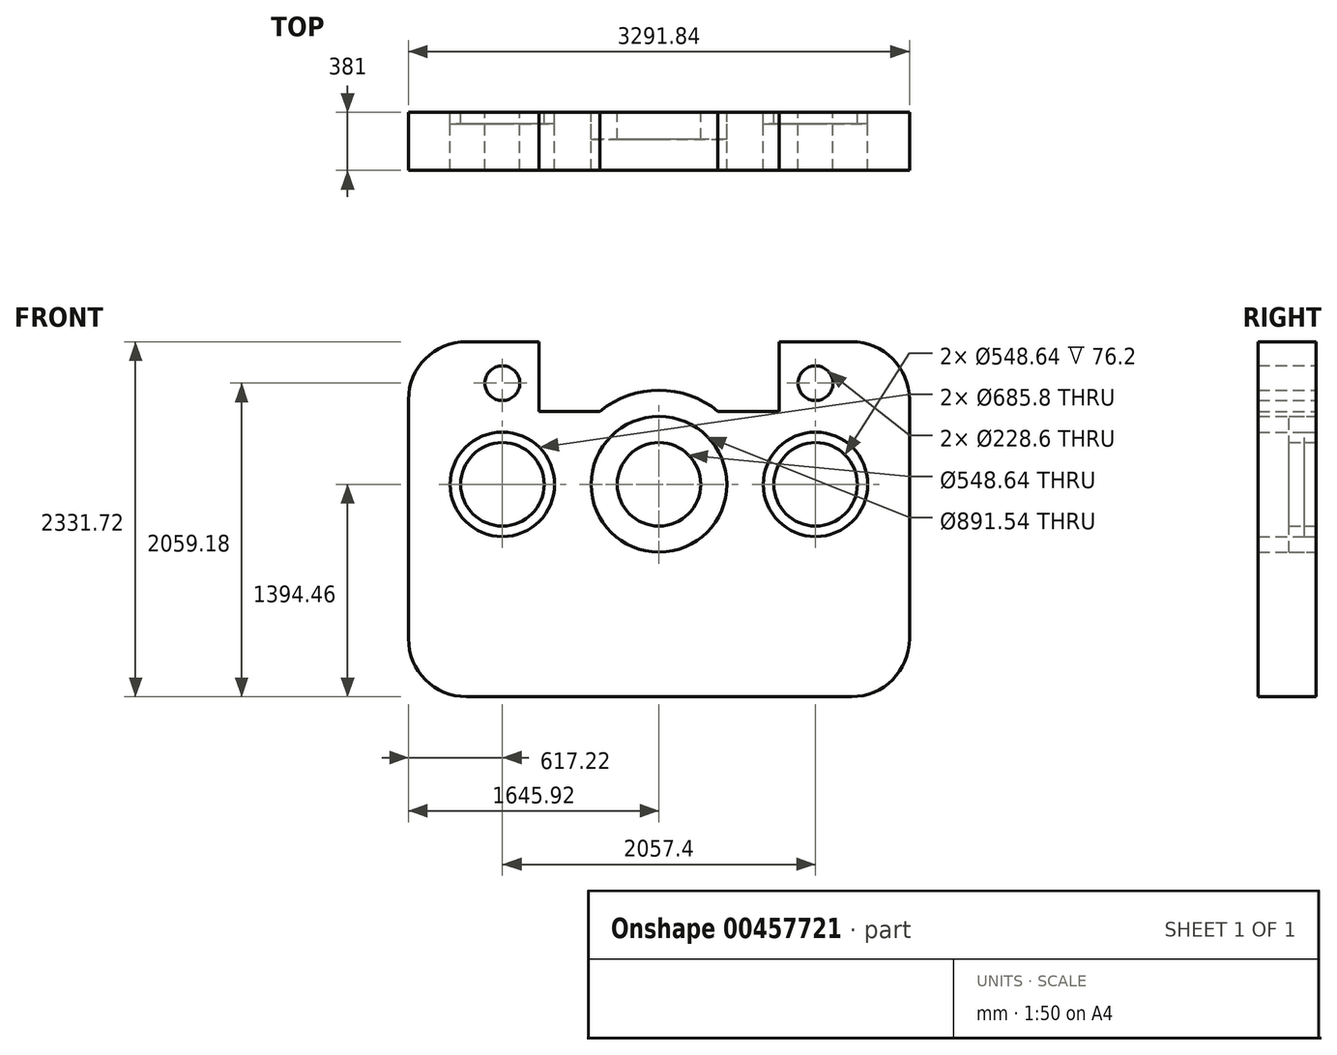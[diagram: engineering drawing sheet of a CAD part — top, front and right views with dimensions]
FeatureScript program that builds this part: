
annotation { "Feature Type Name" : "Feature", "Feature Type Description" : "" }
export const myFeature = defineFeature(function(context is Context, id is Id, definition is map)
    precondition{}
    {
        {
            var Q0;
            Q0=qCreatedBy(makeId("Front.planeOp"),FACE);
            var sketch = newSketch(context, id + "F0", { "sketchPlane" : qUnion([Q0])});
            skLineSegment(sketch, "E0", {"start": v(0, 381) * mm, "end": v(0, 1950.72) * mm});
            skLineSegment(sketch, "E1", {"start": v(381, 0) * mm, "end": v(2910.84, 0) * mm});
            skLineSegment(sketch, "E2", {"start": v(3291.84, 381) * mm, "end": v(3291.84, 1950.72) * mm});
            skArc(sketch, "E3", {"start": v(0, 381) * mm, "mid": v(111.6, 111.6) * mm, "end": v(381, 0) * mm});
            skArc(sketch, "E4", {"start": v(2910.84, 0) * mm, "mid": v(3180.25, 111.6) * mm, "end": v(3291.84, 381) * mm});
            skArc(sketch, "E5", {"start": v(381, 2331.72) * mm, "mid": v(111.6, 2220.13) * mm, "end": v(0, 1950.72) * mm});
            skArc(sketch, "E6", {"start": v(3291.84, 1950.72) * mm, "mid": v(3180.25, 2220.13) * mm, "end": v(2910.84, 2331.72) * mm});
            skLineSegment(sketch, "E7", {"start": v(381, 2331.72) * mm, "end": v(857.25, 2331.72) * mm});
            skLineSegment(sketch, "E8", {"start": v(2910.84, 2331.72) * mm, "end": v(2434.6, 2331.72) * mm});
            skLineSegment(sketch, "E9", {"start": v(857.25, 2331.72) * mm, "end": v(857.25, 1874.52) * mm});
            skLineSegment(sketch, "E10", {"start": v(2434.6, 2331.72) * mm, "end": v(2434.6, 1874.52) * mm});
            skLineSegment(sketch, "E11", {"start": v(2434.6, 1874.52) * mm, "end": v(2033.87, 1874.52) * mm});
            skLineSegment(sketch, "E12", {"start": v(0, 1950.72) * mm, "end": v(0, 1394.46) * mm});
            skArc(sketch, "E13", {"start": v(2033.87, 1874.52) * mm, "mid": v(1645.92, 2011.68) * mm, "end": v(1257.97, 1874.52) * mm});
            skCircle(sketch, "E14", {"center": v(1645.92, 1394.46) * mm, "radius": 274.32 * mm});
            skCircle(sketch, "E15", {"center": v(1645.92, 1394.46) * mm, "radius": 445.77 * mm});
            skLineSegment(sketch, "E16.trimOffspring", {"start": v(1257.97, 1874.52) * mm, "end": v(857.25, 1874.52) * mm});
            skLineSegment(sketch, "E17", {"start": v(381, 2331.72) * mm, "end": v(617.22, 2331.72) * mm});
            skLineSegment(sketch, "E18", {"start": v(2910.84, 2331.72) * mm, "end": v(2674.62, 2331.72) * mm});
            skCircle(sketch, "E19", {"center": v(617.22, 1394.46) * mm, "radius": 342.9 * mm});
            skCircle(sketch, "E20", {"center": v(617.22, 1394.46) * mm, "radius": 274.32 * mm});
            skCircle(sketch, "E21", {"center": v(2674.62, 1394.46) * mm, "radius": 274.32 * mm});
            skCircle(sketch, "E22", {"center": v(2674.62, 1394.46) * mm, "radius": 342.9 * mm});
            skLineSegment(sketch, "E23", {"start": v(3291.84, 2059.18) * mm, "end": v(3276.08, 2059.18) * mm});
            skCircle(sketch, "E24", {"center": v(617.22, 2059.18) * mm, "radius": 114.3 * mm});
            skCircle(sketch, "E25", {"center": v(2674.62, 2059.18) * mm, "radius": 114.3 * mm});
            skSolve(sketch);
        }
        {
            var Q0;
            Q0=makeQuery(id+"F0.imprint","IMPRINT",FACE,{"disambiguationData":[TD([[makeQuery(id+"F0.imprint","IMPRINT",EDGE,{"derivedFrom":sQuery(id+"F0.wireOp",EDGE,"E19")}),1.0]])]});
            var Q1;
            Q1=makeQuery(id+"F0.imprint","IMPRINT",FACE,{"disambiguationData":[TD([[makeQuery(id+"F0.imprint","IMPRINT",EDGE,{"derivedFrom":sQuery(id+"F0.wireOp",EDGE,"E21")}),-1.0]])]});
            extrude(context, id + "F1", {"entities" : qUnion([Q0, Q1]), "depth" : 76.2 * mm});
        }
        {
            var Q0;
            Q0=makeQuery(id+"F0.imprint","IMPRINT",FACE,{"disambiguationData":[TD([[makeQuery(id+"F0.imprint","IMPRINT",EDGE,{"derivedFrom":sQuery(id+"F0.wireOp",EDGE,"E14")}),-1.0]])]});
            extrude(context, id + "F2", {"entities" : qUnion([Q0]), "depth" : 177.8 * mm});
        }
        {
            var Q0;
            Q0=makeQuery(id+"F0.imprint","IMPRINT",FACE,{"disambiguationData":[TD([[makeQuery(id+"F0.imprint","IMPRINT",EDGE,{"derivedFrom":sQuery(id+"F0.wireOp",EDGE,"E0")}),-1.0]])]});
            extrude(context, id + "F3", {"entities" : qUnion([Q0]), "depth" : 381 * mm});
        }
    });
